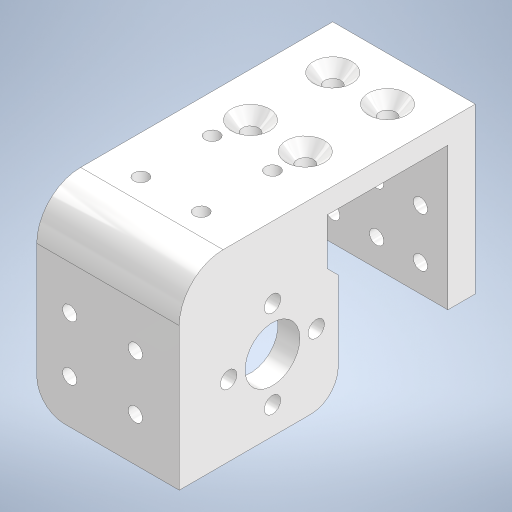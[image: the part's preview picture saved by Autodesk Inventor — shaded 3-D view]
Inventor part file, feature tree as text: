
AUTODESK INVENTOR PART (.ipt)
format: ipt  version: 2024.1 (Build 281209000, 209)  size: 420,352 bytes
history: native  units: mm
features: extrude x11, sketch x11, fillet x3, chamfer x2
ambient origin geometry x8: Origin, YZ Plane, XZ Plane, XY Plane, X Axis, Y Axis, Z Axis, Center Point
bodies: Solid1 (feature_tree)
feature tree (27):
  extrude  "Extrusion1"  Depth=26.0mm
  extrude  "Extrusion2"  Depth=4.0mm
  extrude  "Extrusion3"  Depth=30.0mm TaperAngle=0.0deg
  extrude  "Extrusion4"  Depth=10.0mm
  extrude  "Extrusion6"  TaperAngle=0.0deg  [1 undecoded]
  fillet  "Fillet3"  Radius=3.0mm
  fillet  "Fillet4"  Radius=3.0mm
  fillet  "Fillet5"  Radius=3.0mm
  extrude  "Extrusion7"  Depth=8.0mm
  extrude  "Extrusion8"  Depth=8.0mm
  extrude  "Extrusion9"  Depth=8.0mm
  chamfer  "Chamfer3"  [1 undecoded]
  extrude  "Extrusion10"  Depth=5.0mm
  extrude  "Extrusion11"  Depth=8.0mm
  extrude  "Extrusion13"  Depth=1.5mm
  chamfer  "Chamfer4"  Distance=30.0mm
  sketch  "Sketch1"  dims[d0=45.0mm d1=26.0mm]
  sketch  "Sketch2"  dims[d2=4.0mm d3=0.0mm d4=4.0mm]
  sketch  "Sketch4"  dims[d5=25.0mm d6=30.0mm d7=0.0mm]
  sketch  "Sketch5"  dims[d8=10.0mm d9=13.0mm]
  sketch  "Sketch9"  dims[d10=13.0mm d11=0.0mm d12=0.0mm d13=3.0mm d14=3.0mm d15=3.0mm]
  sketch  "Sketch10"  dims[d16=3.0mm d17=8.0mm]
  sketch  "Sketch12"  dims[d19=8.0mm d20=8.0mm]
  sketch  "Sketch13"  dims[d21=8.0mm d22=8.0mm]
  sketch  "Sketch14"  dims[d23=8.0mm]
  sketch  "Sketch15"  dims[d24=8.0mm d25=0.0mm d26=0.0mm]
  sketch  "Sketch18"  dims[d39=4.0mm d40=0.0mm d41=5.0mm d42=8.0mm d43=1.5mm d44=30.0mm d45=5.0mm d46=0.0mm d47=2.6mm d48=2.6mm d49=2.6mm d50=2.6mm d51=2.6mm d52=5.0mm d53=5.0mm d54=5.0mm d55=5.0mm d56=7.0mm d57=7.0mm d58=16.0mm d59=5.0mm d60=5.0mm d61=5.0mm d62=10.0mm d63=0.0mm d64=2.6mm d65=16.0mm d66=5.0mm d67=3.0mm d68=3.0mm d69=3.0mm d70=3.0mm d71=10.0mm d72=15.0mm d73=15.0mm d74=8.0mm d75=8.0mm d76=8.0mm d77=8.0mm d78=10.0mm d79=0.0mm d80=0.0mm d81=2.6mm d82=2.6mm d83=2.6mm d84=5.0mm d85=13.0mm d86=13.0mm d87=13.0mm d88=7.0mm d89=16.0mm d90=2.0mm d91=2.0mm d92=45.0deg d93=2.6mm d94=2.6mm d95=2.6mm d96=2.6mm d97=8.0mm d98=8.0mm d99=6.0mm d100=6.0mm d101=8.0mm d102=8.0mm d103=10.0mm d104=10.0mm d105=0.0mm d106=0.0mm d107=2.6mm d108=2.6mm d109=2.6mm d110=2.6mm d111=8.0mm d112=8.0mm d113=7.0mm d114=7.0mm d115=13.0mm d116=13.0mm d117=29.0mm d118=29.0mm d119=10.0mm d120=0.0mm d124=8.5mm d125=2.0mm d126=0.0mm d127=0.0mm d128=2.0mm d129=2.0mm d130=45.0deg]
note: 2 required parameter values undecoded (feature->parameter linkage not recoverable at this tier; creation-order binding heuristic only, values carry confidence <= 0.55)
